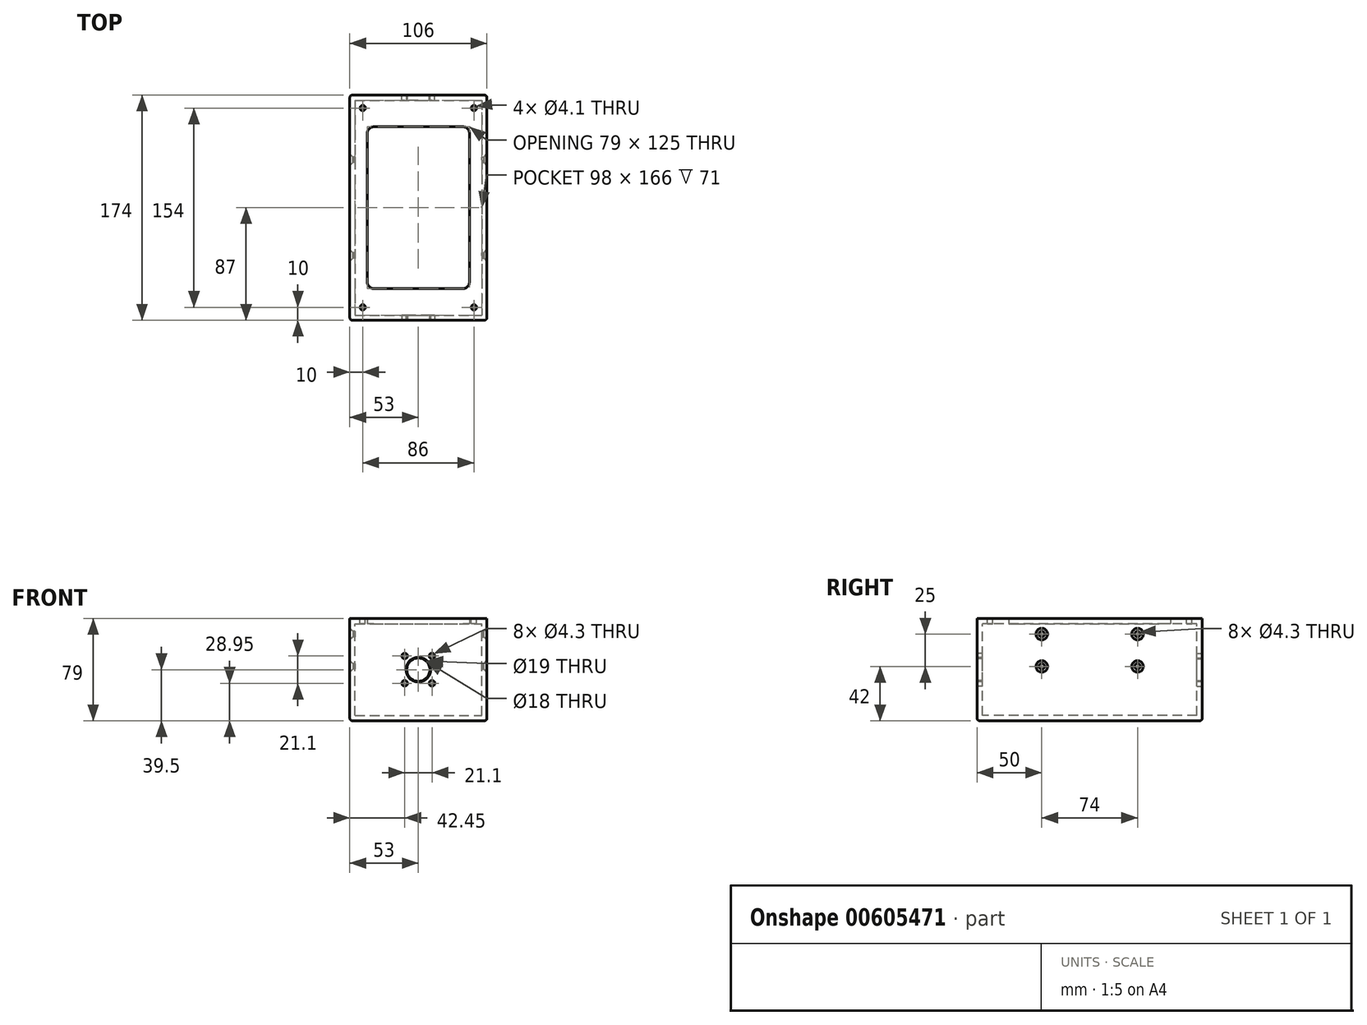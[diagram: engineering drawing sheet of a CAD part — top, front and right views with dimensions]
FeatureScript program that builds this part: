
annotation { "Feature Type Name" : "Feature", "Feature Type Description" : "" }
export const myFeature = defineFeature(function(context is Context, id is Id, definition is map)
    precondition{}
    {
        {
            var Q0;
            Q0=qCreatedBy(makeId("Front.planeOp"),FACE);
            var sketch = newSketch(context, id + "F0", { "sketchPlane" : qUnion([Q0])});
            skLineSegment(sketch, "E0.bottom", {"start": v(0, 0) * mm, "end": v(106, 0) * mm});
            skLineSegment(sketch, "E0.top", {"start": v(0, 75) * mm, "end": v(106, 75) * mm});
            skLineSegment(sketch, "E0.left", {"start": v(0, 0) * mm, "end": v(0, 75) * mm});
            skLineSegment(sketch, "E0.right", {"start": v(106, 0) * mm, "end": v(106, 75) * mm});
            skSolve(sketch);
        }
        {
            var Q0;
            Q0 = qSketchRegion(id + "F0", true);
            extrude(context, id + "F1", {"entities" : qUnion([Q0]), "depth" : 174 * mm, "offsetDistance" : 25 * mm});
        }
        {
            var Q0;
            Q0=makeQuery(id+"F1.opExtrude","SWEPT_FACE",FACE,{"disambiguationData":[OSD([sQuery(id+"F0.wireOp",EDGE,"E0.top")])]});
            var sketch = newSketch(context, id + "F2", { "sketchPlane" : qUnion([Q0])});
            skLineSegment(sketch, "E1.bottom", {"start": v(18.5, -149.5) * mm, "end": v(87.5, -149.5) * mm});
            skLineSegment(sketch, "E1.top", {"start": v(18.5, -24.5) * mm, "end": v(87.5, -24.5) * mm});
            skLineSegment(sketch, "E1.left", {"start": v(13.5, -144.5) * mm, "end": v(13.5, -29.5) * mm});
            skLineSegment(sketch, "E1.right", {"start": v(92.5, -144.5) * mm, "end": v(92.5, -29.5) * mm});
            skLineSegment(sketch, "E2.0", {"start": v(0, -174) * mm, "end": v(0, 0) * mm});
            skLineSegment(sketch, "E3.0", {"start": v(0, 0) * mm, "end": v(106, 0) * mm});
            skLineSegment(sketch, "E4.0", {"start": v(106, -174) * mm, "end": v(106, 0) * mm});
            skLineSegment(sketch, "E5.0", {"start": v(0, -174) * mm, "end": v(106, -174) * mm});
            skPoint(sketch, "E6.visualSharp", {"position": v(13.5, -24.5) * mm});
            skArc(sketch, "E6.filletArc", {"start": v(18.5, -24.5) * mm, "mid": v(14.96, -25.96) * mm, "end": v(13.5, -29.5) * mm});
            skPoint(sketch, "E7.visualSharp", {"position": v(92.5, -24.5) * mm});
            skArc(sketch, "E7.filletArc", {"start": v(92.5, -29.5) * mm, "mid": v(91.04, -25.96) * mm, "end": v(87.5, -24.5) * mm});
            skPoint(sketch, "E8.visualSharp", {"position": v(13.5, -149.5) * mm});
            skArc(sketch, "E8.filletArc", {"start": v(13.5, -144.5) * mm, "mid": v(14.96, -148.04) * mm, "end": v(18.5, -149.5) * mm});
            skPoint(sketch, "E9.visualSharp", {"position": v(92.5, -149.5) * mm});
            skArc(sketch, "E9.filletArc", {"start": v(87.5, -149.5) * mm, "mid": v(91.04, -148.04) * mm, "end": v(92.5, -144.5) * mm});
            skSolve(sketch);
        }
        {
            var Q0;
            Q0 = qSketchRegion(id + "F2", true);
            extrude(context, id + "F3", {"entities" : qUnion([Q0]), "operationType" : NewBodyOperationType.ADD, "depth" : 4 * mm, "offsetDistance" : 25 * mm});
        }
        {
            var Q0;
            Q0=makeQuery(id+"F1.opExtrude","SWEPT_FACE",FACE,{"disambiguationData":[OSD([sQuery(id+"F0.wireOp",EDGE,"E0.top")])]});
            var sketch = newSketch(context, id + "F4", { "sketchPlane" : qUnion([Q0])});
            skLineSegment(sketch, "E10.bottom", {"start": v(4, -4) * mm, "end": v(102, -4) * mm});
            skLineSegment(sketch, "E10.top", {"start": v(4, -170) * mm, "end": v(102, -170) * mm});
            skLineSegment(sketch, "E10.left", {"start": v(4, -4) * mm, "end": v(4, -170) * mm});
            skLineSegment(sketch, "E10.right", {"start": v(102, -4) * mm, "end": v(102, -170) * mm});
            skSolve(sketch);
        }
        {
            var Q0;
            Q0 = qSketchRegion(id + "F4", true);
            extrude(context, id + "F5", {"entities" : qUnion([Q0]), "operationType" : NewBodyOperationType.REMOVE, "oppositeDirection" : true, "depth" : 71 * mm, "offsetDistance" : 25 * mm});
        }
        {
            var Q0;
            Q0=makeQuery(id+"F3.boolean.opBoolean","MERGE",FACE,{"derivedFrom":[makeQuery(id+"F1.opExtrude","SWEPT_FACE",FACE,{"disambiguationData":[OSD([sQuery(id+"F0.wireOp",EDGE,"E0.right")])]}),makeQuery(id+"F3.opExtrude","SWEPT_FACE",FACE,{"disambiguationData":[OSD([sQuery(id+"F2.wireOp",EDGE,"E4.0")])]})]});
            var sketch = newSketch(context, id + "F6", { "sketchPlane" : qUnion([Q0])});
            skLineSegment(sketch, "E11", {"start": v(-87, 79) * mm, "end": v(-87, 0) * mm});
            skPoint(sketch, "E12", {"position": v(-124, 67) * mm});
            skPoint(sketch, "E13", {"position": v(-124, 42) * mm});
            skPoint(sketch, "E14.MirrorP", {"position": v(-50, 67) * mm});
            skPoint(sketch, "E15.MirrorP", {"position": v(-50, 42) * mm});
            skSolve(sketch);
        }
        {
            var Q0;
            Q0=sQuery(id+"F6.wireOp",VERTEX,"E12");
            var Q1;
            Q1=sQuery(id+"F6.wireOp",VERTEX,"E13");
            var Q2;
            Q2=sQuery(id+"F6.wireOp",VERTEX,"E14.MirrorP");
            var Q3;
            Q3=sQuery(id+"F6.wireOp",VERTEX,"E15.MirrorP");
            var Q4;
            Q4=makeQuery(id+"F1.opExtrude","SWEPT_BODY",BODY,{"disambiguationData":[OSD([sQuery(id+"F0.wireOp",EDGE,"E0.bottom"),sQuery(id+"F0.wireOp",EDGE,"E0.top"),sQuery(id+"F0.wireOp",EDGE,"E0.left"),sQuery(id+"F0.wireOp",EDGE,"E0.right")])]});
            hole(context, id + "F7", {"style" : HoleStyle.C_SINK, "endStyle" : HoleEndStyle.BLIND, "holeDiameter" : 4.3 * mm, "cSinkDiameter" : 9 * mm, "cSinkAngle" : 90 * degree, "majorDiameter" : 5 * mm, "holeDepth" : 30 * mm, "isTappedThrough" : true, "tappedDepth" : 12 * mm, "tapClearance" : 3, "locations" : qUnion([Q0, Q1, Q2, Q3]), "scope" : qUnion([Q4])});
        }
        {
            var Q0;
            Q0=makeQuery(id+"F3.boolean.opBoolean","MERGE",FACE,{"derivedFrom":[makeQuery(id+"F1.opExtrude","SWEPT_FACE",FACE,{"disambiguationData":[OSD([sQuery(id+"F0.wireOp",EDGE,"E0.left")])]}),makeQuery(id+"F3.opExtrude","SWEPT_FACE",FACE,{"disambiguationData":[OSD([sQuery(id+"F2.wireOp",EDGE,"E2.0")])]})]});
            var sketch = newSketch(context, id + "F8", { "sketchPlane" : qUnion([Q0])});
            skPoint(sketch, "E16.0", {"position": v(50, 67) * mm});
            skPoint(sketch, "E17.0", {"position": v(50, 42) * mm});
            skPoint(sketch, "E18.0", {"position": v(124, 67) * mm});
            skPoint(sketch, "E19.0", {"position": v(124, 42) * mm});
            skSolve(sketch);
        }
        {
            var Q0;
            Q0=makeQuery(id+"F3.boolean.opBoolean","MERGE",FACE,{"derivedFrom":[makeQuery(id+"F1.opExtrude","CAP_FACE",FACE,{"disambiguationData":[OSD([sQuery(id+"F0.wireOp",EDGE,"E0.bottom"),sQuery(id+"F0.wireOp",EDGE,"E0.top"),sQuery(id+"F0.wireOp",EDGE,"E0.left"),sQuery(id+"F0.wireOp",EDGE,"E0.right")])],"isStart":false}),makeQuery(id+"F3.opExtrude","SWEPT_FACE",FACE,{"disambiguationData":[OSD([sQuery(id+"F2.wireOp",EDGE,"E5.0")])]})]});
            var sketch = newSketch(context, id + "F9", { "sketchPlane" : qUnion([Q0])});
            skPoint(sketch, "E20", {"position": v(42.45, 50.05) * mm});
            skLineSegment(sketch, "E21", {"start": v(0, 39.5) * mm, "end": v(106, 39.5) * mm});
            skLineSegment(sketch, "E22", {"start": v(53, 79) * mm, "end": v(53, 0) * mm});
            skPoint(sketch, "E23.MirrorP", {"position": v(63.55, 50.05) * mm});
            skPoint(sketch, "E24.MirrorP", {"position": v(42.45, 28.95) * mm});
            skPoint(sketch, "E25.MirrorP", {"position": v(63.55, 28.95) * mm});
            skLineSegment(sketch, "E26.bottom", {"start": v(39.85, 52.65) * mm, "end": v(66.15, 52.65) * mm});
            skLineSegment(sketch, "E26.top", {"start": v(39.85, 26.35) * mm, "end": v(66.15, 26.35) * mm});
            skLineSegment(sketch, "E26.left", {"start": v(39.85, 52.65) * mm, "end": v(39.85, 26.35) * mm});
            skLineSegment(sketch, "E26.right", {"start": v(66.15, 52.65) * mm, "end": v(66.15, 26.35) * mm});
            skPoint(sketch, "E27", {"position": v(53, 52.65) * mm});
            skPoint(sketch, "E28", {"position": v(53, 26.35) * mm});
            skPoint(sketch, "E29", {"position": v(66.15, 39.5) * mm});
            skPoint(sketch, "E30", {"position": v(53, 39.5) * mm});
            skSolve(sketch);
        }
        {
            var Q0;
            Q0=sQuery(id+"F9.wireOp",VERTEX,"E20");
            var Q1;
            Q1=sQuery(id+"F9.wireOp",VERTEX,"E24.MirrorP");
            var Q2;
            Q2=sQuery(id+"F9.wireOp",VERTEX,"E23.MirrorP");
            var Q3;
            Q3=sQuery(id+"F9.wireOp",VERTEX,"E25.MirrorP");
            var Q4;
            Q4=makeQuery(id+"F1.opExtrude","SWEPT_BODY",BODY,{"disambiguationData":[OSD([sQuery(id+"F0.wireOp",EDGE,"E0.bottom"),sQuery(id+"F0.wireOp",EDGE,"E0.top"),sQuery(id+"F0.wireOp",EDGE,"E0.left"),sQuery(id+"F0.wireOp",EDGE,"E0.right")])]});
            hole(context, id + "F10", {"style" : HoleStyle.SIMPLE, "endStyle" : HoleEndStyle.BLIND, "holeDiameter" : 4.3 * mm, "majorDiameter" : 5 * mm, "holeDepth" : 30 * mm, "isTappedThrough" : true, "tappedDepth" : 12 * mm, "tapClearance" : 3, "locations" : qUnion([Q0, Q1, Q2, Q3]), "scope" : qUnion([Q4])});
        }
        {
            var Q0;
            Q0=makeQuery(id+"F3.boolean.opBoolean","MERGE",FACE,{"derivedFrom":[makeQuery(id+"F1.opExtrude","CAP_FACE",FACE,{"disambiguationData":[OSD([sQuery(id+"F0.wireOp",EDGE,"E0.bottom"),sQuery(id+"F0.wireOp",EDGE,"E0.top"),sQuery(id+"F0.wireOp",EDGE,"E0.left"),sQuery(id+"F0.wireOp",EDGE,"E0.right")])],"isStart":true}),makeQuery(id+"F3.opExtrude","SWEPT_FACE",FACE,{"disambiguationData":[OSD([sQuery(id+"F2.wireOp",EDGE,"E3.0")])]})]});
            var sketch = newSketch(context, id + "F11", { "sketchPlane" : qUnion([Q0])});
            skPoint(sketch, "E31.0", {"position": v(-63.55, 50.05) * mm});
            skPoint(sketch, "E32.0", {"position": v(-63.55, 28.95) * mm});
            skPoint(sketch, "E33.0", {"position": v(-42.45, 50.05) * mm});
            skPoint(sketch, "E34.0", {"position": v(-42.45, 28.95) * mm});
            skSolve(sketch);
        }
        {
            var Q0;
            Q0=sQuery(id+"F11.wireOp",VERTEX,"E31.0");
            var Q1;
            Q1=sQuery(id+"F11.wireOp",VERTEX,"E32.0");
            var Q2;
            Q2=sQuery(id+"F11.wireOp",VERTEX,"E33.0");
            var Q3;
            Q3=sQuery(id+"F11.wireOp",VERTEX,"E34.0");
            var Q4;
            Q4=makeQuery(id+"F1.opExtrude","SWEPT_BODY",BODY,{"disambiguationData":[OSD([sQuery(id+"F0.wireOp",EDGE,"E0.bottom"),sQuery(id+"F0.wireOp",EDGE,"E0.top"),sQuery(id+"F0.wireOp",EDGE,"E0.left"),sQuery(id+"F0.wireOp",EDGE,"E0.right")])]});
            hole(context, id + "F12", {"style" : HoleStyle.SIMPLE, "endStyle" : HoleEndStyle.BLIND, "holeDiameter" : 4.3 * mm, "majorDiameter" : 5 * mm, "holeDepth" : 30 * mm, "isTappedThrough" : true, "tappedDepth" : 12 * mm, "tapClearance" : 3, "locations" : qUnion([Q0, Q1, Q2, Q3]), "scope" : qUnion([Q4])});
        }
        {
            var Q0;
            Q0=sQuery(id+"F8.wireOp",VERTEX,"E16.0");
            var Q1;
            Q1=sQuery(id+"F8.wireOp",VERTEX,"E17.0");
            var Q2;
            Q2=sQuery(id+"F8.wireOp",VERTEX,"E18.0");
            var Q3;
            Q3=sQuery(id+"F8.wireOp",VERTEX,"E19.0");
            var Q4;
            Q4=makeQuery(id+"F1.opExtrude","SWEPT_BODY",BODY,{"disambiguationData":[OSD([sQuery(id+"F0.wireOp",EDGE,"E0.bottom"),sQuery(id+"F0.wireOp",EDGE,"E0.top"),sQuery(id+"F0.wireOp",EDGE,"E0.left"),sQuery(id+"F0.wireOp",EDGE,"E0.right")])]});
            hole(context, id + "F13", {"style" : HoleStyle.C_SINK, "endStyle" : HoleEndStyle.BLIND, "holeDiameter" : 4.3 * mm, "cSinkDiameter" : 9 * mm, "cSinkAngle" : 90 * degree, "majorDiameter" : 5 * mm, "holeDepth" : 30 * mm, "isTappedThrough" : true, "tappedDepth" : 12 * mm, "tapClearance" : 3, "locations" : qUnion([Q0, Q1, Q2, Q3]), "scope" : qUnion([Q4])});
        }
        {
            var Q0;
            Q0=makeQuery(id+"F3.opExtrude","CAP_FACE",FACE,{"disambiguationData":[OSD([sQuery(id+"F2.wireOp",EDGE,"E1.bottom"),sQuery(id+"F2.wireOp",EDGE,"E1.top"),sQuery(id+"F2.wireOp",EDGE,"E1.left"),sQuery(id+"F2.wireOp",EDGE,"E1.right"),sQuery(id+"F2.wireOp",EDGE,"E2.0"),sQuery(id+"F2.wireOp",EDGE,"E3.0"),sQuery(id+"F2.wireOp",EDGE,"E4.0"),sQuery(id+"F2.wireOp",EDGE,"E5.0"),sQuery(id+"F2.wireOp",EDGE,"E6.filletArc"),sQuery(id+"F2.wireOp",EDGE,"E7.filletArc"),sQuery(id+"F2.wireOp",EDGE,"E8.filletArc"),sQuery(id+"F2.wireOp",EDGE,"E9.filletArc")])],"isStart":false});
            var sketch = newSketch(context, id + "F14", { "sketchPlane" : qUnion([Q0])});
            skPoint(sketch, "E35", {"position": v(10, -10) * mm});
            skLineSegment(sketch, "E36", {"start": v(53, 0) * mm, "end": v(53, -174) * mm, "construction": true});
            skLineSegment(sketch, "E37", {"start": v(0, -87) * mm, "end": v(106, -87) * mm, "construction": true});
            skPoint(sketch, "E38.MirrorP", {"position": v(96, -10) * mm});
            skPoint(sketch, "E39.MirrorP", {"position": v(10, -164) * mm});
            skPoint(sketch, "E40.MirrorP", {"position": v(96, -164) * mm});
            skSolve(sketch);
        }
        {
            var Q0;
            Q0=sQuery(id+"F14.wireOp",VERTEX,"E35");
            var Q1;
            Q1=sQuery(id+"F14.wireOp",VERTEX,"E38.MirrorP");
            var Q2;
            Q2=sQuery(id+"F14.wireOp",VERTEX,"E39.MirrorP");
            var Q3;
            Q3=sQuery(id+"F14.wireOp",VERTEX,"E40.MirrorP");
            var Q4;
            Q4=makeQuery(id+"F1.opExtrude","SWEPT_BODY",BODY,{"disambiguationData":[OSD([sQuery(id+"F0.wireOp",EDGE,"E0.bottom"),sQuery(id+"F0.wireOp",EDGE,"E0.top"),sQuery(id+"F0.wireOp",EDGE,"E0.left"),sQuery(id+"F0.wireOp",EDGE,"E0.right")])]});
            hole(context, id + "F15", {"style" : HoleStyle.SIMPLE, "endStyle" : HoleEndStyle.BLIND, "holeDiameter" : 4.1 * mm, "majorDiameter" : 5 * mm, "holeDepth" : 30 * mm, "isTappedThrough" : true, "tappedDepth" : 12 * mm, "tapClearance" : 3, "locations" : qUnion([Q0, Q1, Q2, Q3]), "scope" : qUnion([Q4])});
        }
        {
            var Q0;
            Q0=sQuery(id+"F9.wireOp",VERTEX,"E30");
            var Q1;
            Q1=makeQuery(id+"F1.opExtrude","SWEPT_BODY",BODY,{"disambiguationData":[OSD([sQuery(id+"F0.wireOp",EDGE,"E0.bottom"),sQuery(id+"F0.wireOp",EDGE,"E0.top"),sQuery(id+"F0.wireOp",EDGE,"E0.left"),sQuery(id+"F0.wireOp",EDGE,"E0.right")])]});
            hole(context, id + "F16", {"style" : HoleStyle.SIMPLE, "endStyle" : HoleEndStyle.BLIND, "holeDiameter" : 19 * mm, "majorDiameter" : 5 * mm, "holeDepth" : 40 * mm, "isTappedThrough" : true, "tappedDepth" : 12 * mm, "tapClearance" : 3, "locations" : qUnion([Q0]), "scope" : qUnion([Q1])});
        }
        {
            var Q0;
            Q0=makeQuery(id+"F3.boolean.opBoolean","MERGE",FACE,{"derivedFrom":[makeQuery(id+"F1.opExtrude","CAP_FACE",FACE,{"disambiguationData":[OSD([sQuery(id+"F0.wireOp",EDGE,"E0.bottom"),sQuery(id+"F0.wireOp",EDGE,"E0.top"),sQuery(id+"F0.wireOp",EDGE,"E0.left"),sQuery(id+"F0.wireOp",EDGE,"E0.right")])],"isStart":true}),makeQuery(id+"F3.opExtrude","SWEPT_FACE",FACE,{"disambiguationData":[OSD([sQuery(id+"F2.wireOp",EDGE,"E3.0")])]})]});
            var sketch = newSketch(context, id + "F17", { "sketchPlane" : qUnion([Q0])});
            skPoint(sketch, "E41.0", {"position": v(-53, 39.5) * mm});
            skSolve(sketch);
        }
        {
            var Q0;
            Q0=sQuery(id+"F17.wireOp",VERTEX,"E41.0");
            var Q1;
            Q1=makeQuery(id+"F1.opExtrude","SWEPT_BODY",BODY,{"disambiguationData":[OSD([sQuery(id+"F0.wireOp",EDGE,"E0.bottom"),sQuery(id+"F0.wireOp",EDGE,"E0.top"),sQuery(id+"F0.wireOp",EDGE,"E0.left"),sQuery(id+"F0.wireOp",EDGE,"E0.right")])]});
            hole(context, id + "F18", {"style" : HoleStyle.SIMPLE, "endStyle" : HoleEndStyle.BLIND, "holeDiameter" : 18 * mm, "majorDiameter" : 5 * mm, "holeDepth" : 40 * mm, "isTappedThrough" : true, "tappedDepth" : 12 * mm, "tapClearance" : 3, "locations" : qUnion([Q0]), "scope" : qUnion([Q1])});
        }
        {
            var Q0;
            Q0=makeQuery(id+"F3.boolean.opBoolean","MERGE",EDGE,{"derivedFrom":[makeQuery(id+"F1.opExtrude","CAP_EDGE",EDGE,{"disambiguationData":[OSD([sQuery(id+"F0.wireOp",EDGE,"E0.left")])],"isStart":true}),makeQuery(id+"F3.opExtrude","SWEPT_EDGE",EDGE,{"disambiguationData":[OSD([sQuery(id+"F2.wireOp",EDGE,"E2.0"),sQuery(id+"F2.wireOp",EDGE,"E3.0")])]})]});
            var Q1;
            Q1=makeQuery(id+"F3.boolean.opBoolean","MERGE",EDGE,{"derivedFrom":[makeQuery(id+"F1.opExtrude","CAP_EDGE",EDGE,{"disambiguationData":[OSD([sQuery(id+"F0.wireOp",EDGE,"E0.right")])],"isStart":true}),makeQuery(id+"F3.opExtrude","SWEPT_EDGE",EDGE,{"disambiguationData":[OSD([sQuery(id+"F2.wireOp",EDGE,"E3.0"),sQuery(id+"F2.wireOp",EDGE,"E4.0")])]})]});
            var Q2;
            Q2=makeQuery(id+"F3.boolean.opBoolean","MERGE",EDGE,{"derivedFrom":[makeQuery(id+"F1.opExtrude","CAP_EDGE",EDGE,{"disambiguationData":[OSD([sQuery(id+"F0.wireOp",EDGE,"E0.right")])],"isStart":false}),makeQuery(id+"F3.opExtrude","SWEPT_EDGE",EDGE,{"disambiguationData":[OSD([sQuery(id+"F2.wireOp",EDGE,"E4.0"),sQuery(id+"F2.wireOp",EDGE,"E5.0")])]})]});
            var Q3;
            Q3=makeQuery(id+"F3.boolean.opBoolean","MERGE",EDGE,{"derivedFrom":[makeQuery(id+"F1.opExtrude","CAP_EDGE",EDGE,{"disambiguationData":[OSD([sQuery(id+"F0.wireOp",EDGE,"E0.left")])],"isStart":false}),makeQuery(id+"F3.opExtrude","SWEPT_EDGE",EDGE,{"disambiguationData":[OSD([sQuery(id+"F2.wireOp",EDGE,"E2.0"),sQuery(id+"F2.wireOp",EDGE,"E5.0")])]})]});
            var Q4;
            Q4=makeQuery(id+"F1.opExtrude","CAP_EDGE",EDGE,{"disambiguationData":[OSD([sQuery(id+"F0.wireOp",EDGE,"E0.bottom")])],"isStart":false});
            var Q5;
            Q5=makeQuery(id+"F1.opExtrude","SWEPT_EDGE",EDGE,{"disambiguationData":[OSD([sQuery(id+"F0.wireOp",EDGE,"E0.bottom"),sQuery(id+"F0.wireOp",EDGE,"E0.left")])]});
            var Q6;
            Q6=makeQuery(id+"F1.opExtrude","CAP_EDGE",EDGE,{"disambiguationData":[OSD([sQuery(id+"F0.wireOp",EDGE,"E0.bottom")])],"isStart":true});
            var Q7;
            Q7=makeQuery(id+"F1.opExtrude","SWEPT_EDGE",EDGE,{"disambiguationData":[OSD([sQuery(id+"F0.wireOp",EDGE,"E0.bottom"),sQuery(id+"F0.wireOp",EDGE,"E0.right")])]});
            fillet(context, id + "F19", {"entities" : qUnion([Q0, Q1, Q2, Q3, Q4, Q5, Q6, Q7]), "radius" : 2 * mm, "tangentPropagation" : true, "allowEdgeOverflow" : false});
        }
    });
